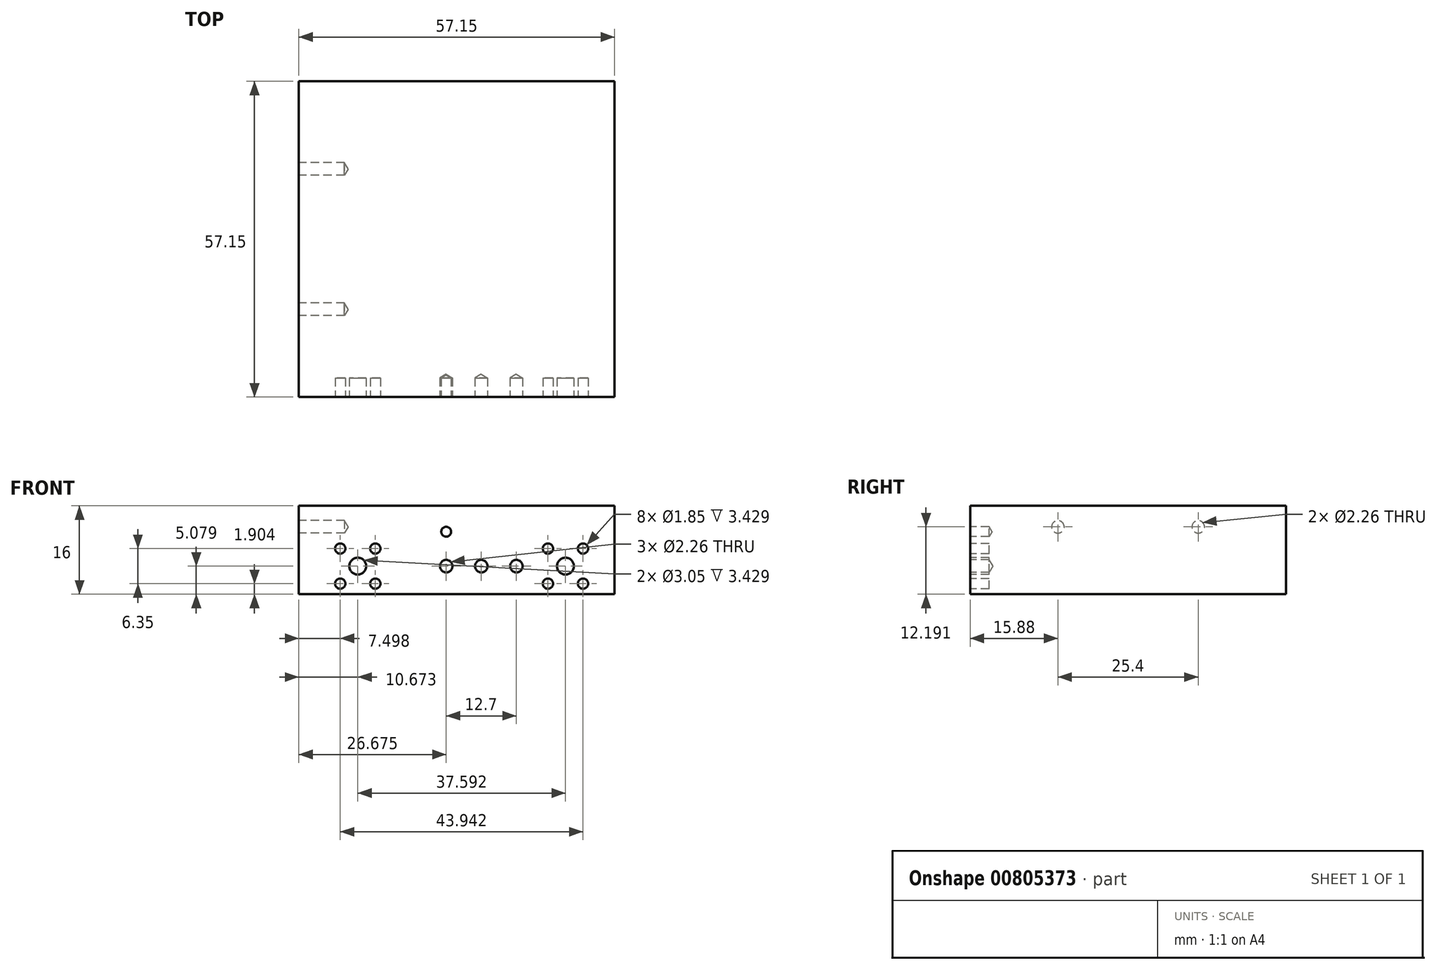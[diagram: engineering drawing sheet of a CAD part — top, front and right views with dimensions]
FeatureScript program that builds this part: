
annotation { "Feature Type Name" : "Feature", "Feature Type Description" : "" }
export const myFeature = defineFeature(function(context is Context, id is Id, definition is map)
    precondition{}
    {
        {
            var Q0;
            Q0=qCreatedBy(makeId("Top.planeOp"),FACE);
            var sketch = newSketch(context, id + "F0", { "sketchPlane" : qUnion([Q0])});
            skLineSegment(sketch, "E0.bottom", {"start": v(-28.57, 28.57) * mm, "end": v(28.58, 28.57) * mm});
            skLineSegment(sketch, "E0.top", {"start": v(-28.57, -28.58) * mm, "end": v(28.58, -28.58) * mm});
            skLineSegment(sketch, "E0.left", {"start": v(-28.57, 28.57) * mm, "end": v(-28.57, -28.58) * mm});
            skLineSegment(sketch, "E0.right", {"start": v(28.58, 28.57) * mm, "end": v(28.58, -28.58) * mm});
            skLineSegment(sketch, "E1", {"start": v(-28.58, -28.58) * mm, "end": v(28.58, 28.57) * mm, "construction": true});
            skSolve(sketch);
        }
        {
            var Q0;
            Q0=makeQuery(id+"F0.imprint","IMPRINT",FACE,{"disambiguationData":[TD([[makeQuery(id+"F0.imprint","IMPRINT",EDGE,{"derivedFrom":sQuery(id+"F0.wireOp",EDGE,"E0.bottom")}),-1.0]])]});
            extrude(context, id + "F1", {"entities" : qUnion([Q0]), "endBound" : BoundingType.SYMMETRIC, "depth" : 16 * mm, "offsetDistance" : 25.4 * mm});
        }
        {
            var Q0;
            Q0=makeQuery(id+"F1.opExtrude","SWEPT_FACE",FACE,{"disambiguationData":[OSD([sQuery(id+"F0.wireOp",EDGE,"E0.top")])]});
            var sketch = newSketch(context, id + "F2", { "sketchPlane" : qUnion([Q0])});
            skCircle(sketch, "E2", {"center": v(-17.9, -2.92) * mm, "radius": 1.52 * mm});
            skCircle(sketch, "E3", {"center": v(19.69, -2.92) * mm, "radius": 1.52 * mm});
            skSolve(sketch);
        }
        {
            var Q0;
            Q0 = qSketchRegion(id + "F2", true);
            extrude(context, id + "F3", {"entities" : qUnion([Q0]), "operationType" : NewBodyOperationType.REMOVE, "oppositeDirection" : true, "depth" : 3.43 * mm, "offsetDistance" : 25.4 * mm});
        }
        {
            var Q0;
            Q0=makeQuery(id+"F1.opExtrude","SWEPT_FACE",FACE,{"disambiguationData":[OSD([sQuery(id+"F0.wireOp",EDGE,"E0.left")])]});
            var sketch = newSketch(context, id + "F4", { "sketchPlane" : qUnion([Q0])});
            skPoint(sketch, "E4", {"position": v(12.7, 4.2) * mm});
            skLineSegment(sketch, "E5", {"start": v(0, 8) * mm, "end": v(0, -8) * mm, "construction": true});
            skPoint(sketch, "E6.MirrorP", {"position": v(-12.7, 4.2) * mm});
            skSolve(sketch);
        }
        {
            var Q0;
            Q0=sQuery(id+"F4.wireOp",VERTEX,"E4");
            var Q1;
            Q1=sQuery(id+"F4.wireOp",VERTEX,"E6.MirrorP");
            var Q2;
            Q2=makeQuery(id+"F1.opExtrude","SWEPT_BODY",BODY,{"disambiguationData":[OSD([sQuery(id+"F0.wireOp",EDGE,"E0.bottom"),sQuery(id+"F0.wireOp",EDGE,"E0.top"),sQuery(id+"F0.wireOp",EDGE,"E0.left"),sQuery(id+"F0.wireOp",EDGE,"E0.right")])]});
            hole(context, id + "F5", {"style" : HoleStyle.SIMPLE, "endStyle" : HoleEndStyle.BLIND, "standardTappedOrClearance" : lookupTablePath({ "standard" : "ANSI", "engagement" : "75%", "pitch" : "40 tpi", "size" : "#4", "type" : "Tapped" }), "standardBlindInLast" : lookupTablePath({ "standard" : "ANSI", "engagement" : "75%", "pitch" : "40 tpi", "size" : "#4", "type" : "Tapped" }), "holeDiameter" : 2.26 * mm, "majorDiameter" : 2.84 * mm, "showTappedDepth" : true, "holeDepth" : 8.25 * mm, "tappedDepth" : 6.35 * mm, "tapClearance" : 3, "locations" : qUnion([Q0, Q1]), "scope" : qUnion([Q2])});
        }
        {
            var Q0;
            Q0=makeQuery(id+"F1.opExtrude","SWEPT_FACE",FACE,{"disambiguationData":[OSD([sQuery(id+"F0.wireOp",EDGE,"E0.top")])]});
            var sketch = newSketch(context, id + "F6", { "sketchPlane" : qUnion([Q0])});
            skCircle(sketch, "E7", {"center": v(-21.08, 0.25) * mm, "radius": 0.93 * mm});
            skCircle(sketch, "E8", {"center": v(-21.08, -6.1) * mm, "radius": 0.93 * mm});
            skCircle(sketch, "E9", {"center": v(-14.73, 0.25) * mm, "radius": 0.93 * mm});
            skCircle(sketch, "E10", {"center": v(-14.73, -6.1) * mm, "radius": 0.93 * mm});
            skLineSegment(sketch, "E11", {"start": v(-17.9, -2.92) * mm, "end": v(-28.57, -2.92) * mm, "construction": true});
            skLineSegment(sketch, "E12", {"start": v(-28.57, -2.92) * mm, "end": v(-17.9, -2.92) * mm, "construction": true});
            skLineSegment(sketch, "E13", {"start": v(-17.9, -2.92) * mm, "end": v(-17.9, 8) * mm, "construction": true});
            skCircle(sketch, "E14", {"center": v(16.51, 0.25) * mm, "radius": 0.93 * mm});
            skCircle(sketch, "E15", {"center": v(16.51, -6.1) * mm, "radius": 0.93 * mm});
            skCircle(sketch, "E16", {"center": v(22.86, 0.25) * mm, "radius": 0.93 * mm});
            skCircle(sketch, "E17", {"center": v(22.86, -6.1) * mm, "radius": 0.93 * mm});
            skLineSegment(sketch, "E18", {"start": v(19.69, -2.92) * mm, "end": v(19.69, 8) * mm, "construction": true});
            skLineSegment(sketch, "E19", {"start": v(19.69, -2.92) * mm, "end": v(28.58, -2.92) * mm, "construction": true});
            skSolve(sketch);
        }
        {
            var Q0;
            Q0 = qSketchRegion(id + "F6", true);
            extrude(context, id + "F7", {"entities" : qUnion([Q0]), "operationType" : NewBodyOperationType.REMOVE, "oppositeDirection" : true, "depth" : 3.43 * mm, "offsetDistance" : 25.4 * mm});
        }
        {
            var Q0;
            Q0=makeQuery(id+"F1.opExtrude","SWEPT_FACE",FACE,{"disambiguationData":[OSD([sQuery(id+"F0.wireOp",EDGE,"E0.top")])]});
            var sketch = newSketch(context, id + "F8", { "sketchPlane" : qUnion([Q0])});
            skPoint(sketch, "E20", {"position": v(-1.9, 3.3) * mm});
            skSolve(sketch);
        }
        {
            var Q0;
            Q0=sQuery(id+"F8.wireOp",VERTEX,"E20");
            var Q1;
            Q1=makeQuery(id+"F1.opExtrude","SWEPT_BODY",BODY,{"disambiguationData":[OSD([sQuery(id+"F0.wireOp",EDGE,"E0.bottom"),sQuery(id+"F0.wireOp",EDGE,"E0.top"),sQuery(id+"F0.wireOp",EDGE,"E0.left"),sQuery(id+"F0.wireOp",EDGE,"E0.right")])]});
            hole(context, id + "F9", {"style" : HoleStyle.SIMPLE, "endStyle" : HoleEndStyle.BLIND, "standardTappedOrClearance" : lookupTablePath({ "standard" : "ANSI", "engagement" : "75%", "pitch" : "56 tpi", "size" : "#2", "type" : "Tapped" }), "standardBlindInLast" : lookupTablePath({ "standard" : "ANSI", "engagement" : "75%", "pitch" : "56 tpi", "size" : "#2", "type" : "Tapped" }), "holeDiameter" : 1.78 * mm, "majorDiameter" : 2.18 * mm, "showTappedDepth" : true, "holeDepth" : 3.43 * mm, "isTappedThrough" : true, "tappedDepth" : 2.07 * mm, "tapClearance" : 3, "locations" : qUnion([Q0]), "scope" : qUnion([Q1])});
        }
        {
            var Q0;
            Q0=makeQuery(id+"F1.opExtrude","SWEPT_FACE",FACE,{"disambiguationData":[OSD([sQuery(id+"F0.wireOp",EDGE,"E0.top")])]});
            var sketch = newSketch(context, id + "F10", { "sketchPlane" : qUnion([Q0])});
            skPoint(sketch, "E21", {"position": v(-1.9, -2.92) * mm});
            skPoint(sketch, "E22", {"position": v(4.45, -2.92) * mm});
            skPoint(sketch, "E23", {"position": v(10.8, -2.92) * mm});
            skSolve(sketch);
        }
        {
            var Q0;
            Q0=sQuery(id+"F10.wireOp",VERTEX,"E21");
            var Q1;
            Q1=sQuery(id+"F10.wireOp",VERTEX,"E22");
            var Q2;
            Q2=sQuery(id+"F10.wireOp",VERTEX,"E23");
            var Q3;
            Q3=makeQuery(id+"F1.opExtrude","SWEPT_BODY",BODY,{"disambiguationData":[OSD([sQuery(id+"F0.wireOp",EDGE,"E0.bottom"),sQuery(id+"F0.wireOp",EDGE,"E0.top"),sQuery(id+"F0.wireOp",EDGE,"E0.left"),sQuery(id+"F0.wireOp",EDGE,"E0.right")])]});
            hole(context, id + "F11", {"style" : HoleStyle.SIMPLE, "endStyle" : HoleEndStyle.BLIND, "standardTappedOrClearance" : lookupTablePath({ "standard" : "ANSI", "engagement" : "75%", "pitch" : "40 tpi", "size" : "#4", "type" : "Tapped" }), "standardBlindInLast" : lookupTablePath({ "standard" : "ANSI", "engagement" : "75%", "pitch" : "40 tpi", "size" : "#4", "type" : "Tapped" }), "holeDiameter" : 2.26 * mm, "majorDiameter" : 2.84 * mm, "showTappedDepth" : true, "holeDepth" : 3.43 * mm, "isTappedThrough" : true, "tappedDepth" : 1.52 * mm, "tapClearance" : 3, "locations" : qUnion([Q0, Q1, Q2]), "scope" : qUnion([Q3])});
        }
    });
